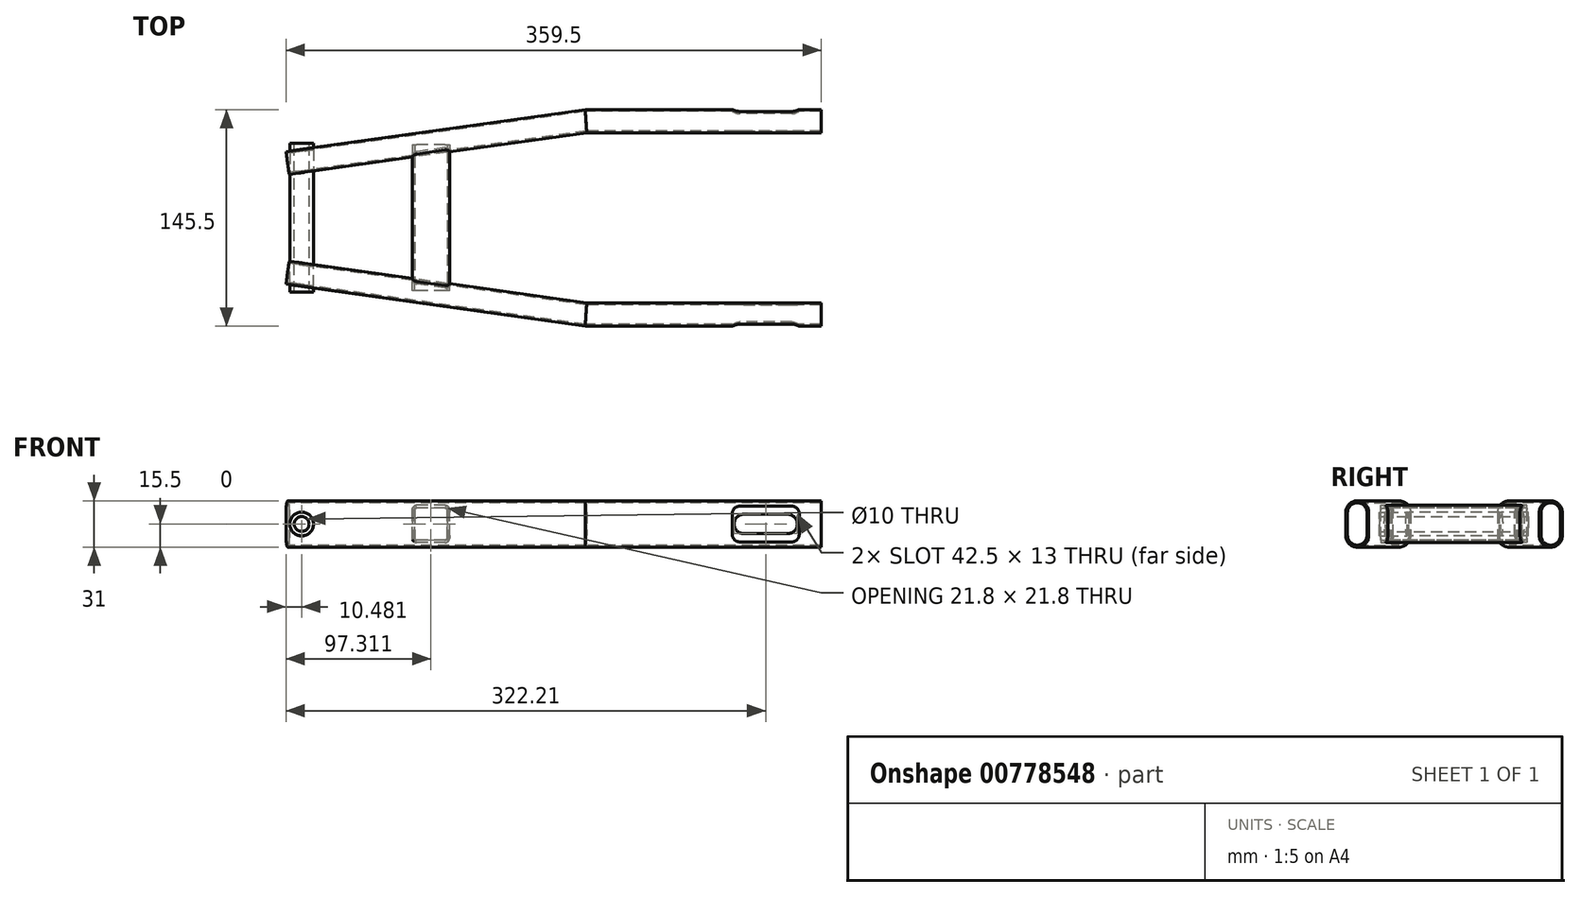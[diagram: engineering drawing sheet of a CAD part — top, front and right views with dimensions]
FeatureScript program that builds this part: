
annotation { "Feature Type Name" : "Feature", "Feature Type Description" : "" }
export const myFeature = defineFeature(function(context is Context, id is Id, definition is map)
    precondition{}
    {
        {
            var Q0;
            Q0=qCreatedBy(makeId("Top.planeOp"),FACE);
            var sketch = newSketch(context, id + "F0", { "sketchPlane" : qUnion([Q0])});
            skLineSegment(sketch, "E0", {"start": v(0, 65) * mm, "end": v(-158.03, 65) * mm});
            skLineSegment(sketch, "E1", {"start": v(-158.03, 65) * mm, "end": v(-358.42, 36.84) * mm});
            skSolve(sketch);
        }
        {
            var Q0;
            Q0=qCreatedBy(makeId("Right.planeOp"),FACE);
            var sketch = newSketch(context, id + "F1", { "sketchPlane" : qUnion([Q0])});
            skLineSegment(sketch, "E2.left", {"start": v(57.25, 7.75) * mm, "end": v(57.25, -7.75) * mm});
            skLineSegment(sketch, "E2.right", {"start": v(72.75, 7.75) * mm, "end": v(72.75, -7.75) * mm});
            skPoint(sketch, "E2.middle", {"position": v(65, 0) * mm});
            skArc(sketch, "E3", {"start": v(57.25, 7.75) * mm, "mid": v(65, 15.5) * mm, "end": v(72.75, 7.75) * mm});
            skArc(sketch, "E4", {"start": v(72.75, -7.75) * mm, "mid": v(65, -15.5) * mm, "end": v(57.25, -7.75) * mm});
            skLineSegment(sketch, "E5.0", {"start": v(71.55, 7.75) * mm, "end": v(71.55, -7.75) * mm});
            skLineSegment(sketch, "E6.0", {"start": v(58.45, 7.75) * mm, "end": v(58.45, -7.75) * mm});
            skArc(sketch, "E7.0", {"start": v(58.45, 7.75) * mm, "mid": v(65, 14.3) * mm, "end": v(71.55, 7.75) * mm});
            skArc(sketch, "E8.0", {"start": v(71.55, -7.75) * mm, "mid": v(65, -14.3) * mm, "end": v(58.45, -7.75) * mm});
            skSolve(sketch);
        }
        {
            var Q0;
            Q0 = qSketchRegion(id + "F1", true);
            var Q1;
            Q1 = qConstructionFilter(qBodyType(qCreatedBy(id + "F0" ,EDGE), BodyType.WIRE), ConstructionObject.NO);
            sweep(context, id + "F2", {"profiles" : qUnion([Q0]), "path" : qUnion([Q1])});
        }
        {
            var Q0;
            Q0=makeQuery(id+"F2.opSweep","SWEPT_FACE",FACE,{"disambiguationData":[OSD([sQuery(id+"F0.wireOp",EDGE,"E0"),sQuery(id+"F1.wireOp",EDGE,"E2.left")])]});
            var sketch = newSketch(context, id + "F3", { "sketchPlane" : qUnion([Q0])});
            skLineSegment(sketch, "E9.bottom", {"start": v(-22.54, -6.5) * mm, "end": v(-52.04, -6.5) * mm});
            skLineSegment(sketch, "E9.top", {"start": v(-22.54, 6.5) * mm, "end": v(-52.04, 6.5) * mm});
            skPoint(sketch, "E9.middle", {"position": v(-37.3, 0) * mm});
            skArc(sketch, "E10", {"start": v(-22.54, 6.5) * mm, "mid": v(-16.04, 0) * mm, "end": v(-22.54, -6.5) * mm});
            skArc(sketch, "E11", {"start": v(-52.04, -6.5) * mm, "mid": v(-58.54, 0) * mm, "end": v(-52.04, 6.5) * mm});
            skSolve(sketch);
        }
        {
            var Q0;
            Q0=makeQuery(id+"F3.imprint","IMPRINT",FACE,{"disambiguationData":[TD([[makeQuery(id+"F3.imprint","IMPRINT",EDGE,{"derivedFrom":sQuery(id+"F3.wireOp",EDGE,"E9.bottom")}),-1.0]])]});
            extrude(context, id + "F4", {"entities" : qUnion([Q0]), "operationType" : NewBodyOperationType.REMOVE, "oppositeDirection" : true, "depth" : 2.7 * mm, "offsetDistance" : 25 * mm});
        }
        {
            var Q0;
            Q0=makeQuery(id+"F2.opSweep","SWEPT_FACE",FACE,{"disambiguationData":[OSD([sQuery(id+"F0.wireOp",EDGE,"E0"),sQuery(id+"F1.wireOp",EDGE,"E2.right")])]});
            var sketch = newSketch(context, id + "F5", { "sketchPlane" : qUnion([Q0])});
            skLineSegment(sketch, "E12.bottom", {"start": v(54.76, -12) * mm, "end": v(19.76, -12) * mm});
            skLineSegment(sketch, "E12.top", {"start": v(54.76, 12) * mm, "end": v(19.76, 12) * mm});
            skLineSegment(sketch, "E12.left", {"start": v(59.76, -7) * mm, "end": v(59.76, 7) * mm});
            skLineSegment(sketch, "E12.right", {"start": v(14.76, -7) * mm, "end": v(14.76, 7) * mm});
            skPoint(sketch, "E12.middle", {"position": v(37.26, 0) * mm});
            skPoint(sketch, "E13.visualSharp", {"position": v(14.76, 12) * mm});
            skArc(sketch, "E13.filletArc", {"start": v(19.76, 12) * mm, "mid": v(16.22, 10.54) * mm, "end": v(14.76, 7) * mm});
            skPoint(sketch, "E14.visualSharp", {"position": v(14.76, -12) * mm});
            skArc(sketch, "E14.filletArc", {"start": v(14.76, -7) * mm, "mid": v(16.22, -10.54) * mm, "end": v(19.76, -12) * mm});
            skPoint(sketch, "E15.visualSharp", {"position": v(59.76, -12) * mm});
            skArc(sketch, "E15.filletArc", {"start": v(54.76, -12) * mm, "mid": v(58.3, -10.54) * mm, "end": v(59.76, -7) * mm});
            skPoint(sketch, "E16.visualSharp", {"position": v(59.76, 12) * mm});
            skArc(sketch, "E16.filletArc", {"start": v(59.76, 7) * mm, "mid": v(58.3, 10.54) * mm, "end": v(54.76, 12) * mm});
            skSolve(sketch);
        }
        {
            var Q0;
            {var subQ11=sQuery(id+"F5.wireOp",EDGE,"E12.left");Q0=makeQuery(id+"F5.imprint","IMPRINT",FACE,{"disambiguationData":[TD([[makeQuery(id+"F5.imprint","IMPRINT",EDGE,{"derivedFrom":subQ11}),1.0]])]});}
            var Q1;
            {var subQ0=sQuery(id+"F5.wireOp",EDGE,"E12.top");Q1=makeQuery(id+"F5.imprint","IMPRINT",FACE,{"disambiguationData":[TD([[makeQuery(id+"F5.imprint","IMPRINT",EDGE,{"derivedFrom":subQ0}),1.0]])]});}
            var Q2;
            {var subQ0=sQuery(id+"F5.wireOp",EDGE,"E12.bottom");Q2=makeQuery(id+"F5.imprint","IMPRINT",FACE,{"disambiguationData":[TD([[makeQuery(id+"F5.imprint","IMPRINT",EDGE,{"derivedFrom":subQ0}),-1.0]])]});}
            extrude(context, id + "F6", {"entities" : qUnion([Q0, Q1, Q2]), "operationType" : NewBodyOperationType.REMOVE, "oppositeDirection" : true, "depth" : 3 * mm, "offsetDistance" : 25 * mm});
        }
        {
            var Q0;
            Q0=qCreatedBy(makeId("Front.planeOp"),FACE);
            var sketch = newSketch(context, id + "F7", { "sketchPlane" : qUnion([Q0])});
            skLineSegment(sketch, "E17.bottom", {"start": v(-252.69, -12.5) * mm, "end": v(-271.69, -12.5) * mm});
            skLineSegment(sketch, "E17.top", {"start": v(-252.69, 12.5) * mm, "end": v(-271.69, 12.5) * mm});
            skLineSegment(sketch, "E17.left", {"start": v(-249.69, -9.5) * mm, "end": v(-249.69, 9.5) * mm});
            skLineSegment(sketch, "E17.right", {"start": v(-274.69, -9.5) * mm, "end": v(-274.69, 9.5) * mm});
            skPoint(sketch, "E17.middle", {"position": v(-262.19, 0) * mm});
            skPoint(sketch, "E18.visualSharp", {"position": v(-274.69, 12.5) * mm});
            skArc(sketch, "E18.filletArc", {"start": v(-271.69, 12.5) * mm, "mid": v(-273.81, 11.62) * mm, "end": v(-274.69, 9.5) * mm});
            skPoint(sketch, "E19.visualSharp", {"position": v(-249.69, 12.5) * mm});
            skArc(sketch, "E19.filletArc", {"start": v(-249.69, 9.5) * mm, "mid": v(-250.57, 11.62) * mm, "end": v(-252.69, 12.5) * mm});
            skPoint(sketch, "E20.visualSharp", {"position": v(-249.69, -12.5) * mm});
            skArc(sketch, "E20.filletArc", {"start": v(-252.69, -12.5) * mm, "mid": v(-250.57, -11.62) * mm, "end": v(-249.69, -9.5) * mm});
            skPoint(sketch, "E21.visualSharp", {"position": v(-274.69, -12.5) * mm});
            skArc(sketch, "E21.filletArc", {"start": v(-274.69, -9.5) * mm, "mid": v(-273.81, -11.62) * mm, "end": v(-271.69, -12.5) * mm});
            skLineSegment(sketch, "E22.0", {"start": v(-252.69, 10.9) * mm, "end": v(-271.69, 10.9) * mm});
            skLineSegment(sketch, "E23.0", {"start": v(-273.09, -9.5) * mm, "end": v(-273.09, 9.5) * mm});
            skLineSegment(sketch, "E24.0", {"start": v(-252.69, -10.9) * mm, "end": v(-271.69, -10.9) * mm});
            skLineSegment(sketch, "E25.0", {"start": v(-251.29, -9.5) * mm, "end": v(-251.29, 9.5) * mm});
            skArc(sketch, "E26", {"start": v(-251.29, 9.5) * mm, "mid": v(-251.7, 10.49) * mm, "end": v(-252.69, 10.9) * mm});
            skArc(sketch, "E27", {"start": v(-271.69, 10.9) * mm, "mid": v(-272.68, 10.49) * mm, "end": v(-273.09, 9.5) * mm});
            skArc(sketch, "E28", {"start": v(-273.09, -9.5) * mm, "mid": v(-272.68, -10.49) * mm, "end": v(-271.69, -10.9) * mm});
            skArc(sketch, "E29", {"start": v(-252.69, -10.9) * mm, "mid": v(-251.7, -10.49) * mm, "end": v(-251.29, -9.5) * mm});
            skSolve(sketch);
        }
        {
            var Q0;
            Q0=makeQuery(id+"F7.imprint","IMPRINT",FACE,{"disambiguationData":[TD([[makeQuery(id+"F7.imprint","IMPRINT",EDGE,{"derivedFrom":sQuery(id+"F7.wireOp",EDGE,"E17.bottom")}),-1.0]])]});
            extrude(context, id + "F8", {"entities" : qUnion([Q0]), "operationType" : NewBodyOperationType.ADD, "oppositeDirection" : true, "depth" : 49 * mm, "offsetDistance" : 25 * mm});
        }
        {
            var Q0;
            Q0=qCreatedBy(makeId("Front.planeOp"),FACE);
            var sketch = newSketch(context, id + "F9", { "sketchPlane" : qUnion([Q0])});
            skCircle(sketch, "E30", {"center": v(-349.02, 0) * mm, "radius": 8 * mm});
            skSolve(sketch);
        }
        {
            var Q0;
            Q0 = qSketchRegion(id + "F9", true);
            extrude(context, id + "F10", {"entities" : qUnion([Q0]), "operationType" : NewBodyOperationType.ADD, "oppositeDirection" : true, "depth" : 50 * mm, "offsetDistance" : 25 * mm});
        }
        {
            var Q0;
            Q0=makeQuery(id+"F10.opExtrude","CAP_FACE",FACE,{"disambiguationData":[OSD([sQuery(id+"F9.wireOp",EDGE,"E30")])],"isStart":false});
            var sketch = newSketch(context, id + "F11", { "sketchPlane" : qUnion([Q0])});
            skCircle(sketch, "E31", {"center": v(349.02, 0) * mm, "radius": 5 * mm});
            skSolve(sketch);
        }
        {
            var Q0;
            Q0 = qSketchRegion(id + "F11", true);
            extrude(context, id + "F12", {"entities" : qUnion([Q0]), "operationType" : NewBodyOperationType.REMOVE, "endBound" : BoundingType.THROUGH_ALL, "oppositeDirection" : true, "depth" : 25 * mm, "offsetDistance" : 25 * mm});
        }
        {
            var Q0;
            Q0=makeQuery(id+"F2.opSweep","SWEPT_BODY",BODY,{"disambiguationData":[OSD([sQuery(id+"F0.wireOp",EDGE,"E1"),sQuery(id+"F1.wireOp",EDGE,"E2.left"),sQuery(id+"F1.wireOp",EDGE,"E2.right"),sQuery(id+"F1.wireOp",EDGE,"E3"),sQuery(id+"F1.wireOp",EDGE,"E4"),sQuery(id+"F1.wireOp",EDGE,"E5.0"),sQuery(id+"F1.wireOp",EDGE,"E6.0"),sQuery(id+"F1.wireOp",EDGE,"E7.0"),sQuery(id+"F1.wireOp",EDGE,"E8.0")])]});
            var Q1;
            Q1=qCreatedBy(makeId("Front.planeOp"),FACE);
            mirror(context, id + "F13", {"operationType" : NewBodyOperationType.ADD, "entities" : qUnion([Q0]), "mirrorPlane" : qUnion([Q1])});
        }
    });
